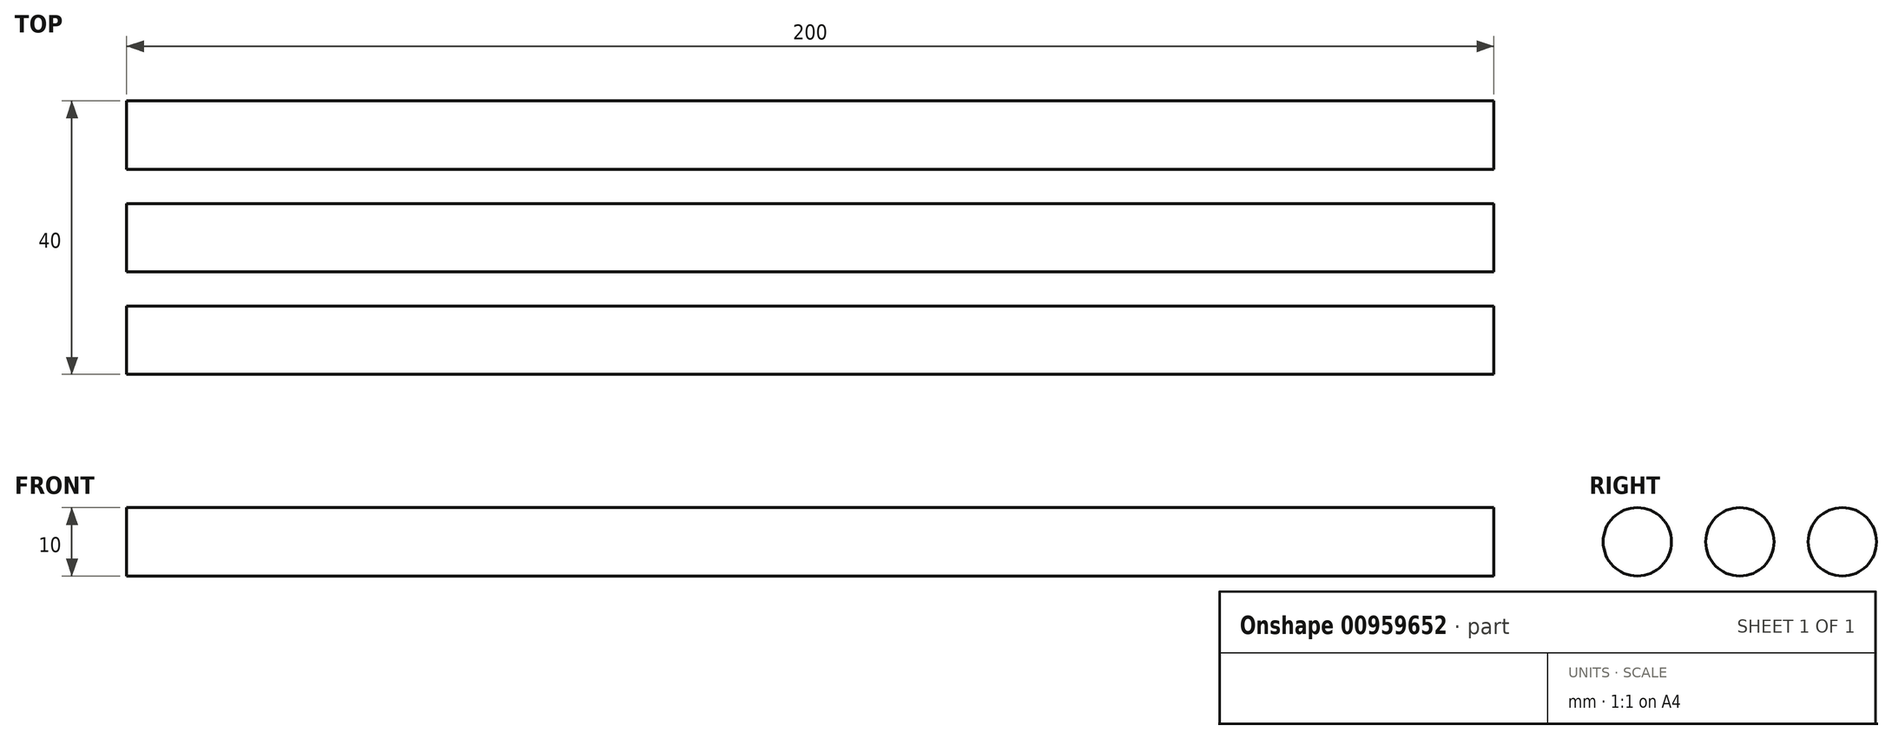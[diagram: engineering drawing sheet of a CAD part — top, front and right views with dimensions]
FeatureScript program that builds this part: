
annotation { "Feature Type Name" : "Feature", "Feature Type Description" : "" }
export const myFeature = defineFeature(function(context is Context, id is Id, definition is map)
    precondition{}
    {
        {
            var Q0;
            Q0=qCreatedBy(makeId("Right.planeOp"),FACE);
            var sketch = newSketch(context, id + "F0", { "sketchPlane" : qUnion([Q0])});
            skCircle(sketch, "E0", {"center": v(0, 0) * mm, "radius": 5 * mm});
            skSolve(sketch);
        }
        {
            var Q0;
            Q0=sQuery(id+"F0.wireOp",EDGE,"E0");
            extrude(context, id + "F1", {"bodyType" : ToolBodyType.SURFACE, "surfaceEntities" : qUnion([Q0]), "endBound" : BoundingType.SYMMETRIC, "depth" : 200 * mm, "offsetDistance" : 25.4 * mm});
        }
        {
            var Q0;
            Q0=makeQuery(id+"F1.opExtrude","SWEPT_BODY",BODY,{"disambiguationData":[OSD([sQuery(id+"F0.wireOp",EDGE,"E0")])]});
            transform(context, id + "F2", {"entities" : qUnion([Q0]), "transformType" : TransformType.TRANSLATION_3D, "dx" : 0 * mm, "dy" : 15 * mm, "dz" : 0 * mm, "makeCopy" : true});
        }
        {
            var Q0;
            Q0=makeQuery(id+"F1.opExtrude","SWEPT_BODY",BODY,{"disambiguationData":[OSD([sQuery(id+"F0.wireOp",EDGE,"E0")])]});
            transform(context, id + "F3", {"entities" : qUnion([Q0]), "transformType" : TransformType.TRANSLATION_3D, "dx" : 0 * mm, "dy" : -15 * mm, "dz" : 0 * mm, "makeCopy" : true});
        }
    });
